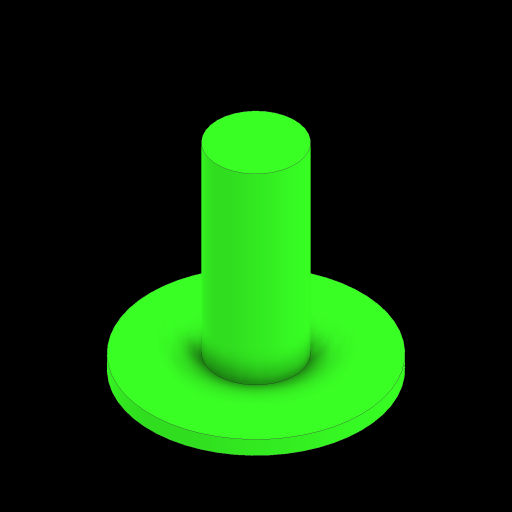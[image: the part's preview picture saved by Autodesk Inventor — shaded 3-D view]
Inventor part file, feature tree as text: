
AUTODESK INVENTOR PART (.ipt)
format: ipt  version: 2023 (Build 270158000, 158)  size: 114,688 bytes
history: native  units: mm
features: extrude x2, sketch x1
ambient origin geometry x8: Origin, YZ Plane, XZ Plane, XY Plane, X Axis, Y Axis, Z Axis, Center Point
bodies: Solid1 (feature_tree)
feature tree (3):
  sketch  "Sketch1"  dims[d0=15.0mm d1=5.5mm d2=1.0mm d3=0.0mm d4=14.0mm d5=0.0mm]
  extrude  "Extrusion1"  Depth=14.0mm
  extrude  "Extrusion2"  Depth=1.0mm TaperAngle=0.0deg
